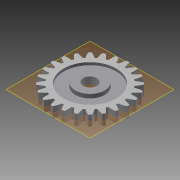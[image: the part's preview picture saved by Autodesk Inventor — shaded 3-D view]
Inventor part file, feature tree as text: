
AUTODESK INVENTOR PART (.ipt)
format: ipt  version: 2014 (Build 180170000, 170)  size: 240,640 bytes
history: native  units: mm
features: other x5, extrude x2, sketch x2, mirror x1
ambient origin geometry x8: Origin, YZ Plane, XZ Plane, XY Plane, X Axis, Y Axis, Z Axis, Center Point
bodies: Body1 (feature_tree)
feature tree (10):
  other  "平歯車1"
  extrude  "押し出し1"  Depth=10.0mm
  extrude  "押し出し2"  Depth=5.2mm
  other  "作業平面1"
  mirror  "ミラー1"
  other  "Solid1::平歯車1"
  other  "TaggingFeature1"
  sketch  "スケッチ1"
  sketch  "スケッチ2"
  other  "ソリッド1"
